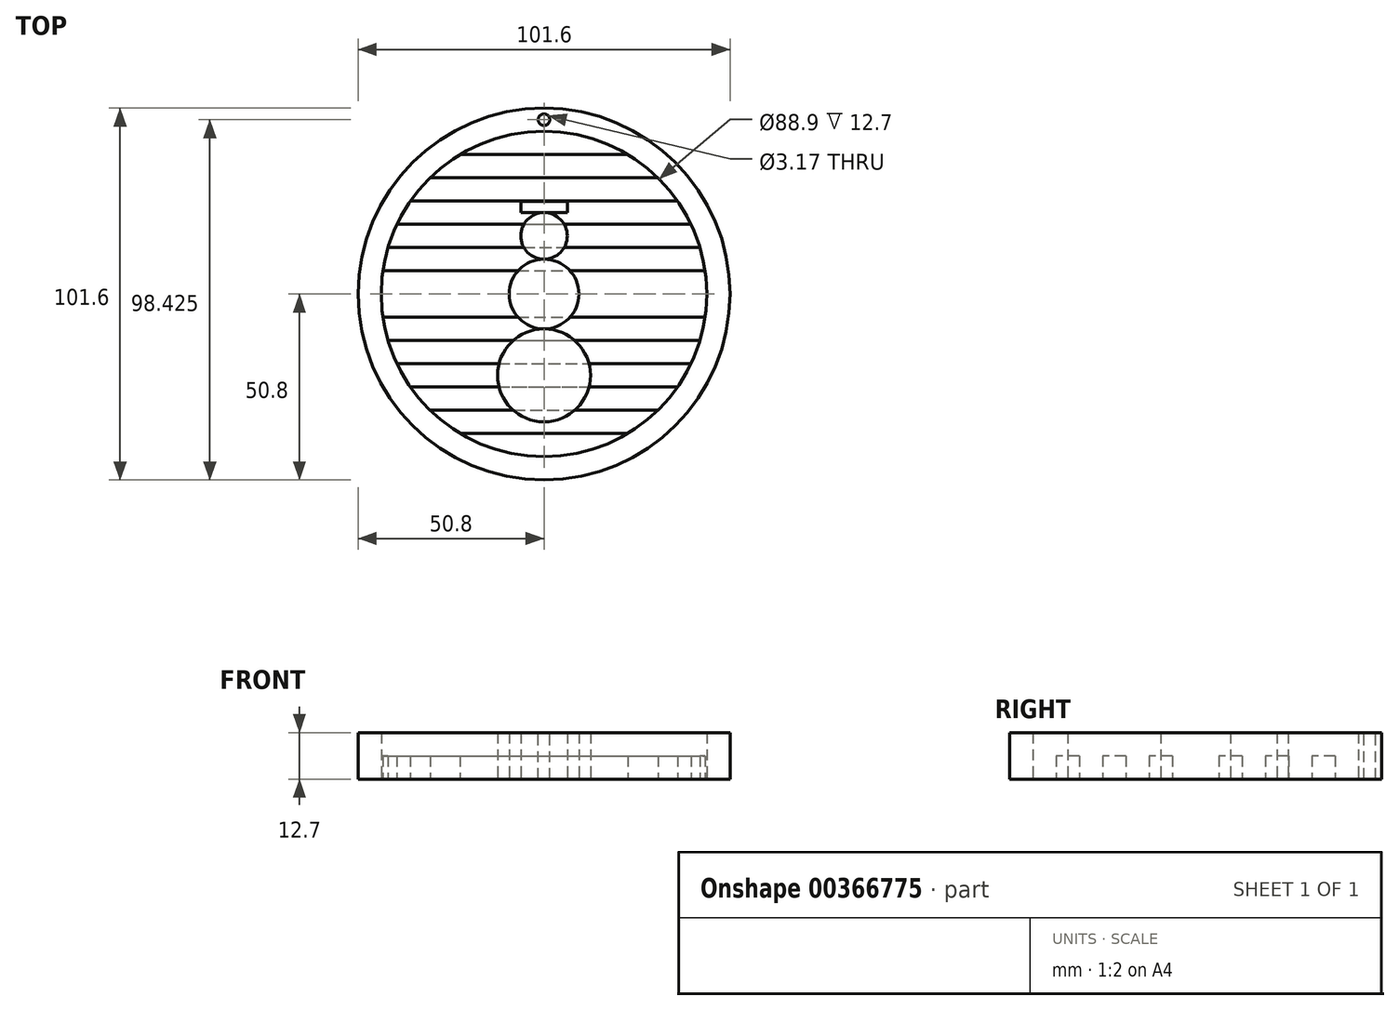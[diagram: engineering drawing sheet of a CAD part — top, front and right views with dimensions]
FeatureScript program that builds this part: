
annotation { "Feature Type Name" : "Feature", "Feature Type Description" : "" }
export const myFeature = defineFeature(function(context is Context, id is Id, definition is map)
    precondition{}
    {
        {
            var Q0;
            Q0=qCreatedBy(makeId("Top.planeOp"),FACE);
            var sketch = newSketch(context, id + "F0", { "sketchPlane" : qUnion([Q0])});
            skCircle(sketch, "E0", {"center": v(0, 0) * mm, "radius": 50.8 * mm});
            skCircle(sketch, "E1", {"center": v(0, 0) * mm, "radius": 44.45 * mm});
            skCircle(sketch, "E2", {"center": v(0, 0) * mm, "radius": 9.53 * mm});
            skCircle(sketch, "E3", {"center": v(0, -22.23) * mm, "radius": 12.7 * mm});
            skCircle(sketch, "E4", {"center": v(0, 15.88) * mm, "radius": 6.35 * mm});
            skLineSegment(sketch, "E5.bottom", {"start": v(6.35, 22.23) * mm, "end": v(-6.35, 22.23) * mm});
            skLineSegment(sketch, "E5.top", {"start": v(6.35, 25.27) * mm, "end": v(-6.35, 25.27) * mm});
            skLineSegment(sketch, "E5.left", {"start": v(6.35, 22.23) * mm, "end": v(6.35, 25.27) * mm});
            skLineSegment(sketch, "E5.right", {"start": v(-6.35, 22.23) * mm, "end": v(-6.35, 25.27) * mm});
            skPoint(sketch, "E5.middle", {"position": v(0, 23.75) * mm});
            skLineSegment(sketch, "E6.bottom", {"start": v(-3.18, 25.27) * mm, "end": v(3.17, 25.27) * mm});
            skLineSegment(sketch, "E6.top", {"start": v(-3.18, 34.16) * mm, "end": v(3.17, 34.16) * mm});
            skLineSegment(sketch, "E6.left", {"start": v(-3.18, 25.27) * mm, "end": v(-3.18, 34.16) * mm});
            skLineSegment(sketch, "E6.right", {"start": v(3.17, 25.27) * mm, "end": v(3.17, 34.16) * mm});
            skPoint(sketch, "E6.middle", {"position": v(0, 29.72) * mm});
            skSolve(sketch);
        }
        {
            var Q0;
            Q0=qCreatedBy(makeId("Top.planeOp"),FACE);
            var sketch = newSketch(context, id + "F1", { "sketchPlane" : qUnion([Q0])});
            skCircle(sketch, "E7.0", {"center": v(0, 0) * mm, "radius": 44.45 * mm});
            skLineSegment(sketch, "E8", {"start": v(-22.9, 38.1) * mm, "end": v(22.9, 38.1) * mm});
            skLineSegment(sketch, "E9", {"start": v(-31.1, 31.75) * mm, "end": v(31.1, 31.75) * mm});
            skLineSegment(sketch, "E10", {"start": v(-36.48, 25.4) * mm, "end": v(36.48, 25.4) * mm});
            skLineSegment(sketch, "E11", {"start": v(-40.16, 19.05) * mm, "end": v(40.16, 19.05) * mm});
            skLineSegment(sketch, "E12", {"start": v(-42.6, 12.7) * mm, "end": v(42.6, 12.7) * mm});
            skLineSegment(sketch, "E13", {"start": v(-44, 6.35) * mm, "end": v(44, 6.35) * mm});
            skLineSegment(sketch, "E14", {"start": v(-44, -6.35) * mm, "end": v(44, -6.35) * mm});
            skLineSegment(sketch, "E15", {"start": v(-42.6, -12.7) * mm, "end": v(42.6, -12.7) * mm});
            skLineSegment(sketch, "E16", {"start": v(-40.16, -19.05) * mm, "end": v(40.16, -19.05) * mm});
            skLineSegment(sketch, "E17", {"start": v(-36.48, -25.4) * mm, "end": v(36.48, -25.4) * mm});
            skLineSegment(sketch, "E18", {"start": v(-31.1, -31.75) * mm, "end": v(31.1, -31.75) * mm});
            skLineSegment(sketch, "E19", {"start": v(-22.9, -38.1) * mm, "end": v(22.9, -38.1) * mm});
            skSolve(sketch);
        }
        {
            var Q0;
            Q0 = qSketchRegion(id + "F0", true);
            var Q1;
            Q1=makeQuery(id+"F0.imprint","IMPRINT",FACE,{"disambiguationData":[TD([[makeQuery(id+"F0.imprint","IMPRINT",EDGE,{"derivedFrom":sQuery(id+"F0.wireOp",EDGE,"E6.bottom")}),1.0]])]});
            var Q2;
            {var subQ3=sQuery(id+"F0.wireOp",EDGE,"E5.left");Q2=makeQuery(id+"F0.imprint","IMPRINT",FACE,{"disambiguationData":[TD([[makeQuery(id+"F0.imprint","IMPRINT",EDGE,{"derivedFrom":subQ3}),1.0]])]});}
            var Q3;
            {var subQ0=sQuery(id+"F0.wireOp",EDGE,"E4");var subQ1=makeQuery(id+"F0.imprint","INTERSECT",VERTEX,{"derivedFrom":[sQuery(id+"F0.wireOp",EDGE,"E2"),subQ0]});Q3=makeQuery(id+"F0.imprint","IMPRINT",FACE,{"disambiguationData":[TD([[makeQuery(id+"F0.imprint","IMPRINT",EDGE,{"disambiguationData":[TD([[subQ1,1.0]])],"derivedFrom":subQ0}),1.0]])]});}
            var Q4;
            {var subQ0=sQuery(id+"F0.wireOp",EDGE,"E2");var subQ1=makeQuery(id+"F0.imprint","INTERSECT",VERTEX,{"derivedFrom":[subQ0,sQuery(id+"F0.wireOp",EDGE,"E3")]});Q4=makeQuery(id+"F0.imprint","IMPRINT",FACE,{"disambiguationData":[TD([[makeQuery(id+"F0.imprint","IMPRINT",EDGE,{"disambiguationData":[TD([[subQ1,1.0]])],"derivedFrom":subQ0}),1.0]])]});}
            var Q5;
            Q5=makeQuery(id+"F0.imprint","IMPRINT",FACE,{"disambiguationData":[TD([[makeQuery(id+"F0.imprint","IMPRINT",EDGE,{"derivedFrom":sQuery(id+"F0.wireOp",EDGE,"E3")}),1.0]])]});
            extrude(context, id + "F2", {"entities" : qUnion([Q0, Q1, Q2, Q3, Q4, Q5]), "depth" : 12.7 * mm});
        }
        {
            var Q0;
            {var subQ0=sQuery(id+"F1.wireOp",EDGE,"E8");Q0=makeQuery(id+"F1.imprint","IMPRINT",FACE,{"disambiguationData":[TD([[makeQuery(id+"F1.imprint","IMPRINT",EDGE,{"derivedFrom":subQ0}),-1.0]])]});}
            var Q1;
            {var subQ0=sQuery(id+"F1.wireOp",EDGE,"E10");Q1=makeQuery(id+"F1.imprint","IMPRINT",FACE,{"disambiguationData":[TD([[makeQuery(id+"F1.imprint","IMPRINT",EDGE,{"derivedFrom":subQ0}),-1.0]])]});}
            var Q2;
            {var subQ0=sQuery(id+"F1.wireOp",EDGE,"E12");Q2=makeQuery(id+"F1.imprint","IMPRINT",FACE,{"disambiguationData":[TD([[makeQuery(id+"F1.imprint","IMPRINT",EDGE,{"derivedFrom":subQ0}),-1.0]])]});}
            var Q3;
            {var subQ0=sQuery(id+"F1.wireOp",EDGE,"E14");Q3=makeQuery(id+"F1.imprint","IMPRINT",FACE,{"disambiguationData":[TD([[makeQuery(id+"F1.imprint","IMPRINT",EDGE,{"derivedFrom":subQ0}),-1.0]])]});}
            var Q4;
            {var subQ0=sQuery(id+"F1.wireOp",EDGE,"E16");Q4=makeQuery(id+"F1.imprint","IMPRINT",FACE,{"disambiguationData":[TD([[makeQuery(id+"F1.imprint","IMPRINT",EDGE,{"derivedFrom":subQ0}),-1.0]])]});}
            var Q5;
            {var subQ0=sQuery(id+"F1.wireOp",EDGE,"E18");Q5=makeQuery(id+"F1.imprint","IMPRINT",FACE,{"disambiguationData":[TD([[makeQuery(id+"F1.imprint","IMPRINT",EDGE,{"derivedFrom":subQ0}),-1.0]])]});}
            extrude(context, id + "F3", {"entities" : qUnion([Q0, Q1, Q2, Q3, Q4, Q5]), "depth" : 6.35 * mm});
        }
        {
            var Q0;
            Q0=makeQuery(id+"F2.opExtrude","CAP_FACE",FACE,{"disambiguationData":[OSD([sQuery(id+"F0.wireOp",EDGE,"E0"),sQuery(id+"F0.wireOp",EDGE,"E1")])],"isStart":false});
            var sketch = newSketch(context, id + "F4", { "sketchPlane" : qUnion([Q0])});
            skCircle(sketch, "E20", {"center": v(0, 47.62) * mm, "radius": 1.59 * mm});
            skSolve(sketch);
        }
        {
            var Q0;
            Q0=makeQuery(id+"F4.imprint","IMPRINT",FACE,{"disambiguationData":[TD([[makeQuery(id+"F4.imprint","IMPRINT",EDGE,{"derivedFrom":sQuery(id+"F4.wireOp",EDGE,"E20")}),1.0]])]});
            extrude(context, id + "F5", {"entities" : qUnion([Q0]), "operationType" : NewBodyOperationType.REMOVE, "oppositeDirection" : true, "depth" : 25.4 * mm});
        }
    });
